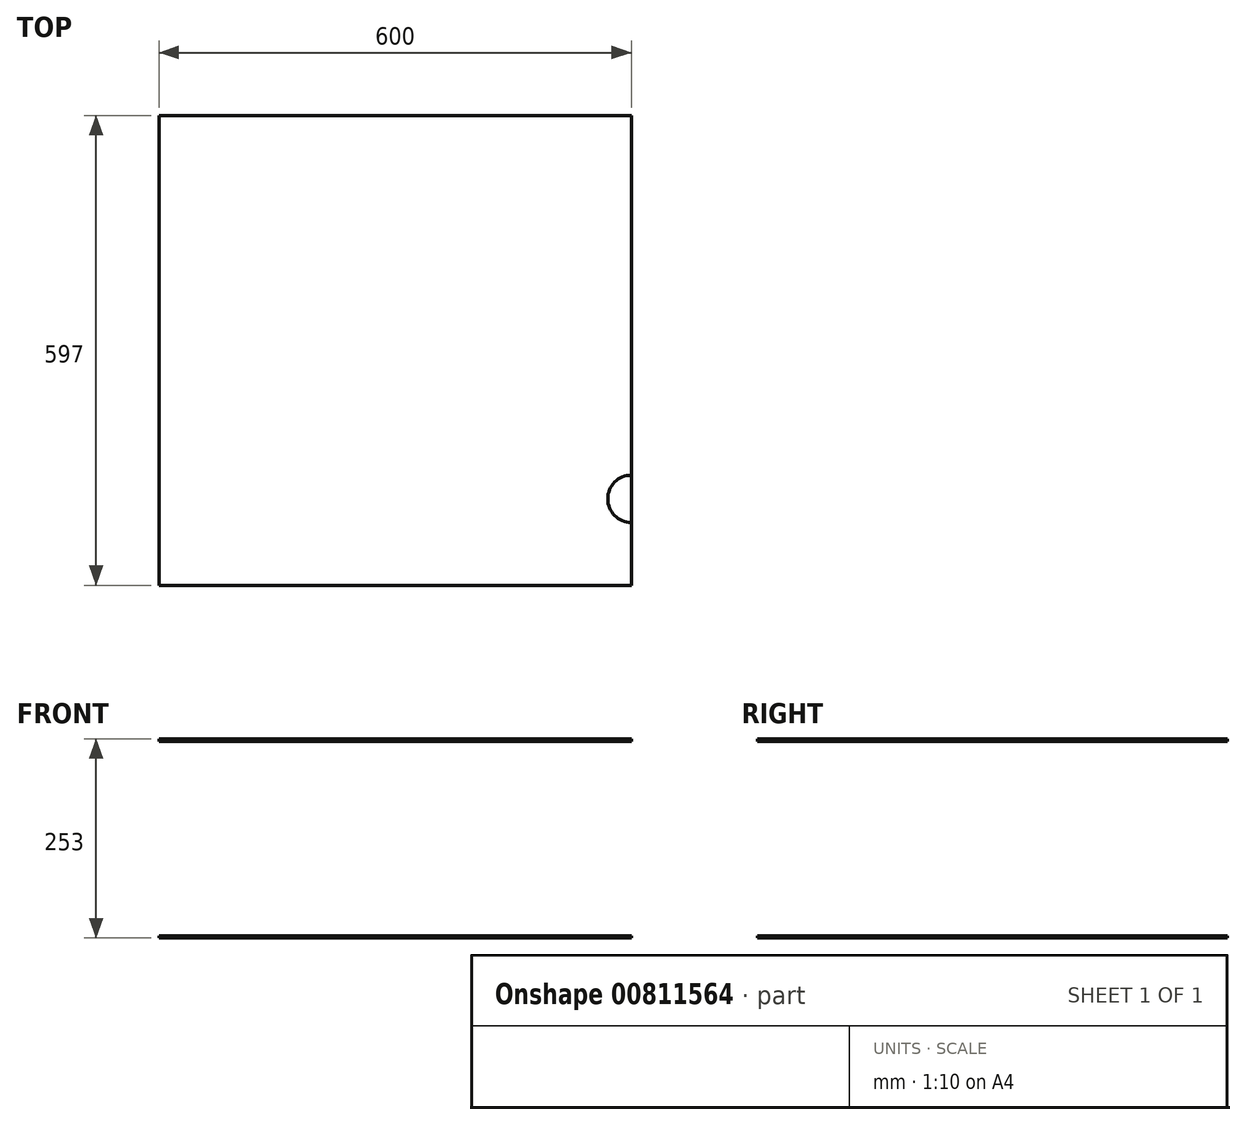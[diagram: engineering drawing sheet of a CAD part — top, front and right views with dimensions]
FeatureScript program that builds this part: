
annotation { "Feature Type Name" : "Feature", "Feature Type Description" : "" }
export const myFeature = defineFeature(function(context is Context, id is Id, definition is map)
    precondition{}
    {
        {
            var Q0;
            Q0=qCreatedBy(makeId("Top.planeOp"),FACE);
            var sketch = newSketch(context, id + "F0", { "sketchPlane" : qUnion([Q0])});
            skLineSegment(sketch, "E0.bottom", {"start": v(300, -298.5) * mm, "end": v(-300, -298.5) * mm});
            skLineSegment(sketch, "E0.top", {"start": v(300, 298.5) * mm, "end": v(-300, 298.5) * mm});
            skLineSegment(sketch, "E0.left", {"start": v(300, -298.5) * mm, "end": v(300, 298.5) * mm});
            skLineSegment(sketch, "E0.right", {"start": v(-300, -298.5) * mm, "end": v(-300, 298.5) * mm});
            skPoint(sketch, "E0.middle", {"position": v(0, 0) * mm});
            skSolve(sketch);
        }
        {
            var Q0;
            Q0 = qSketchRegion(id + "F0", true);
            extrude(context, id + "F1", {"entities" : qUnion([Q0]), "depth" : 3 * mm, "offsetDistance" : 25 * mm});
        }
        {
            var Q0;
            Q0=makeQuery(id+"F1.opExtrude","SWEPT_BODY",BODY,{"disambiguationData":[OSD([sQuery(id+"F0.wireOp",EDGE,"E0.bottom"),sQuery(id+"F0.wireOp",EDGE,"E0.top"),sQuery(id+"F0.wireOp",EDGE,"E0.left"),sQuery(id+"F0.wireOp",EDGE,"E0.right")])]});
            transform(context, id + "F2", {"entities" : qUnion([Q0]), "transformType" : TransformType.TRANSLATION_3D, "dx" : 0 * mm, "dy" : 0 * mm, "dz" : 250 * mm, "makeCopy" : true});
        }
        {
            var Q0;
            Q0=makeQuery(id+"F2.opPattern","COPY",FACE,{"derivedFrom":makeQuery(id+"F1.opExtrude","CAP_FACE",FACE,{"disambiguationData":[OSD([sQuery(id+"F0.wireOp",EDGE,"E0.bottom"),sQuery(id+"F0.wireOp",EDGE,"E0.top"),sQuery(id+"F0.wireOp",EDGE,"E0.left"),sQuery(id+"F0.wireOp",EDGE,"E0.right")])],"isStart":false}),"instanceName":"1"});
            var sketch = newSketch(context, id + "F3", { "sketchPlane" : qUnion([Q0])});
            skLineSegment(sketch, "E1", {"start": v(300, -218.5) * mm, "end": v(300, -158.5) * mm});
            skArc(sketch, "E2", {"start": v(300, -158.5) * mm, "mid": v(270, -188.5) * mm, "end": v(300, -218.5) * mm});
            skSolve(sketch);
        }
        {
            var Q0;
            Q0 = qSketchRegion(id + "F3", true);
            var Q1;
            Q1=makeQuery(id+"F2.opPattern","COPY",FACE,{"derivedFrom":makeQuery(id+"F1.opExtrude","CAP_FACE",FACE,{"disambiguationData":[OSD([sQuery(id+"F0.wireOp",EDGE,"E0.bottom"),sQuery(id+"F0.wireOp",EDGE,"E0.top"),sQuery(id+"F0.wireOp",EDGE,"E0.left"),sQuery(id+"F0.wireOp",EDGE,"E0.right")])],"isStart":true}),"instanceName":"1"});
            extrude(context, id + "F4", {"entities" : qUnion([Q0]), "operationType" : NewBodyOperationType.REMOVE, "endBound" : BoundingType.UP_TO_SURFACE, "oppositeDirection" : true, "depth" : 25 * mm, "endBoundEntityFace" : qUnion([Q1]), "offsetDistance" : 25 * mm});
        }
    });
